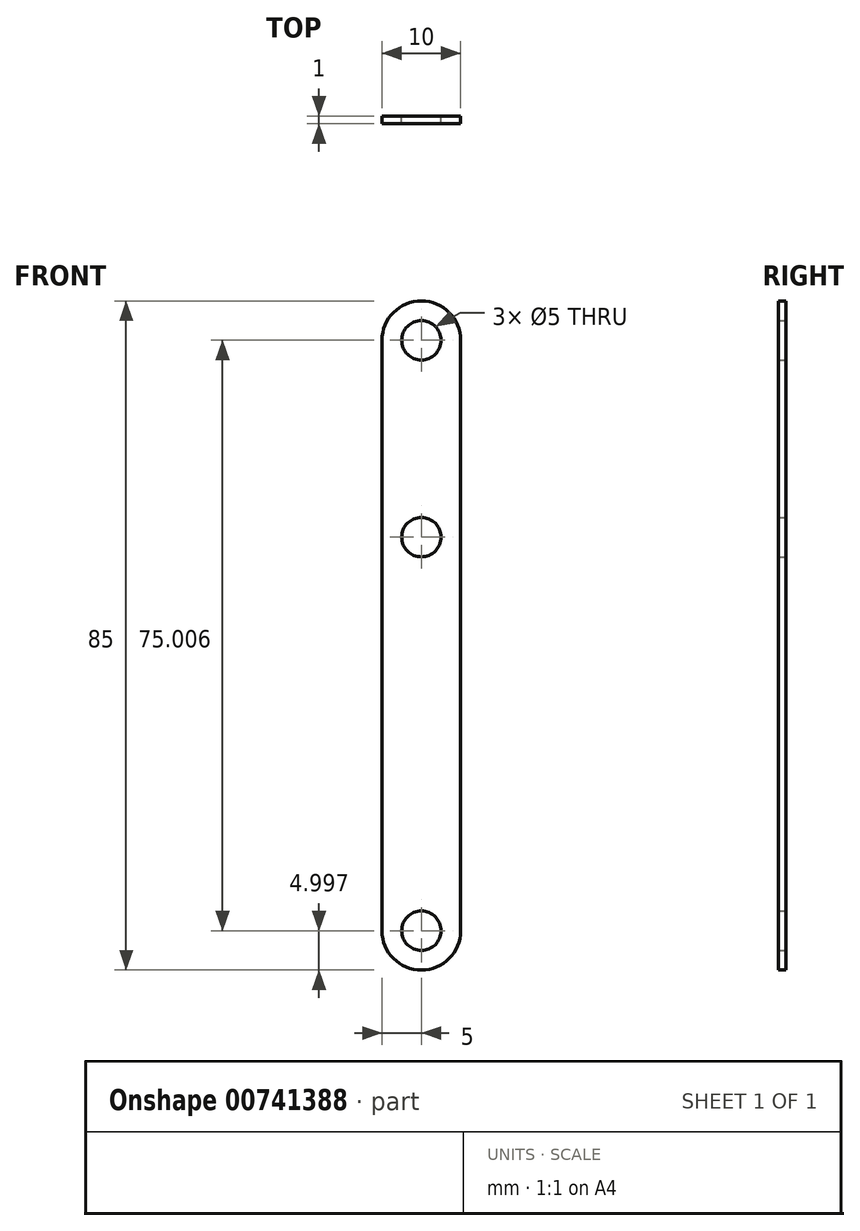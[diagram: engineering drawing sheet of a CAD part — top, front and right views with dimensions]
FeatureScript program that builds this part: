
annotation { "Feature Type Name" : "Feature", "Feature Type Description" : "" }
export const myFeature = defineFeature(function(context is Context, id is Id, definition is map)
    precondition{}
    {
        {
            var Q0;
            Q0=qCreatedBy(makeId("Front.planeOp"),FACE);
            var sketch = newSketch(context, id + "F0", { "sketchPlane" : qUnion([Q0])});
            skLineSegment(sketch, "E0", {"start": v(-8.59, 0) * mm, "end": v(8.84, 0) * mm, "construction": true});
            skCircle(sketch, "E1", {"center": v(0, 37.5) * mm, "radius": 5 * mm});
            skCircle(sketch, "E2", {"center": v(0, 37.5) * mm, "radius": 2.5 * mm});
            skCircle(sketch, "E3.MirrorC", {"center": v(0, -37.5) * mm, "radius": 5 * mm});
            skCircle(sketch, "E4.MirrorC", {"center": v(0, -37.5) * mm, "radius": 2.5 * mm});
            skLineSegment(sketch, "E5", {"start": v(-5, 37.5) * mm, "end": v(-5, -37.5) * mm});
            skLineSegment(sketch, "E6", {"start": v(5, 37.5) * mm, "end": v(5, -37.5) * mm});
            skCircle(sketch, "E7", {"center": v(0, 12.5) * mm, "radius": 2.5 * mm});
            skSolve(sketch);
        }
        {
            var Q0;
            Q0 = qSketchRegion(id + "F0", true);
            extrude(context, id + "F1", {"entities" : qUnion([Q0]), "depth" : 1 * mm, "offsetDistance" : 25.4 * mm});
        }
    });
